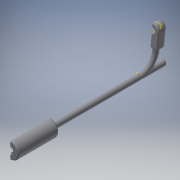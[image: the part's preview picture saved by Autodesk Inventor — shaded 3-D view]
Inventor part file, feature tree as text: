
AUTODESK INVENTOR PART (.ipt)
format: ipt  version: 2018 (Build 220112000, 112)  size: 353,792 bytes
history: native  units: mm
features: sketch x9, extrude x7, fillet x5, projected_geometry x3, plane x2, revolve x1, sweep x1
ambient origin geometry x8: Origin, YZ Plane, XZ Plane, XY Plane, X Axis, Y Axis, Z Axis, Center Point
bodies: Solid1 (feature_tree)
feature tree (28):
  revolve  "Revolution1"  [1 undecoded]
  fillet  "Fillet1"  Radius=8.0mm
  fillet  "Fillet2"  Radius=40.0mm
  fillet  "Fillet3"  [1 undecoded]
  plane  "Work Plane1"
  sweep  "Sweep1"
  extrude  "Extrusion2"  Depth=1.5mm
  fillet  "Fillet4"  Radius=1.0mm
  fillet  "Fillet5"  Radius=1.0mm
  extrude  "Extrusion3"  Depth=1.0mm
  extrude  "Extrusion4"  Depth=6.601018mm
  extrude  "Extrusion5"  Depth=1.0mm
  extrude  "Extrusion6"  [1 undecoded]
  extrude  "Extrusion7"  Depth=18.0mm
  plane  "Work Plane3"
  extrude  "Extrusion8"  TaperAngle=0.0deg  [1 undecoded]
  sketch  "Sketch6"  dims[d0=150.0mm d1=3.0mm d3=8.0mm d4=40.0mm d5=90.0deg]
  sketch  "Sketch8"  dims[d20=1.5mm d21=1.5mm]
  sketch  "Sketch9"  dims[d22=1.5mm d23=1.0mm d24=1.0mm d25=1.0mm]
  projected_geometry  "Projected Loop3"
  sketch  "Sketch10"  dims[d26=1.0mm d27=1.0mm]
  projected_geometry  "Projected Loop4"
  sketch  "Sketch11"  dims[d28=1.456552mm d29=6.601018mm]
  sketch  "Sketch12"  dims[d30=2.0mm d31=1.0mm]
  sketch  "Sketch13"  dims[d32=1.0mm d33=-23.0mm]
  sketch  "Sketch14"  dims[d38=18.0mm d39=18.0mm]
  sketch  "Sketch15"  dims[d40=16.0mm d41=0.0mm d42=0.0mm d43=12.0mm d44=5.0mm d45=6.0mm d46=6.0mm d47=20.0mm d48=0.0mm d49=6.0mm d50=1.0mm d51=3.0mm d52=5.5mm d53=8.0mm d54=0.0mm d55=10.0mm d56=0.0mm d57=50.0mm d58=0.0mm d59=1.4mm d60=0.0mm d61=4.332171mm d62=15.0mm d63=0.0mm d64=-3.0mm d65=6.5mm d66=1.1mm d67=0.0mm]
  projected_geometry  "Projected Loop5"
note: 4 required parameter values undecoded (feature->parameter linkage not recoverable at this tier; creation-order binding heuristic only, values carry confidence <= 0.55)